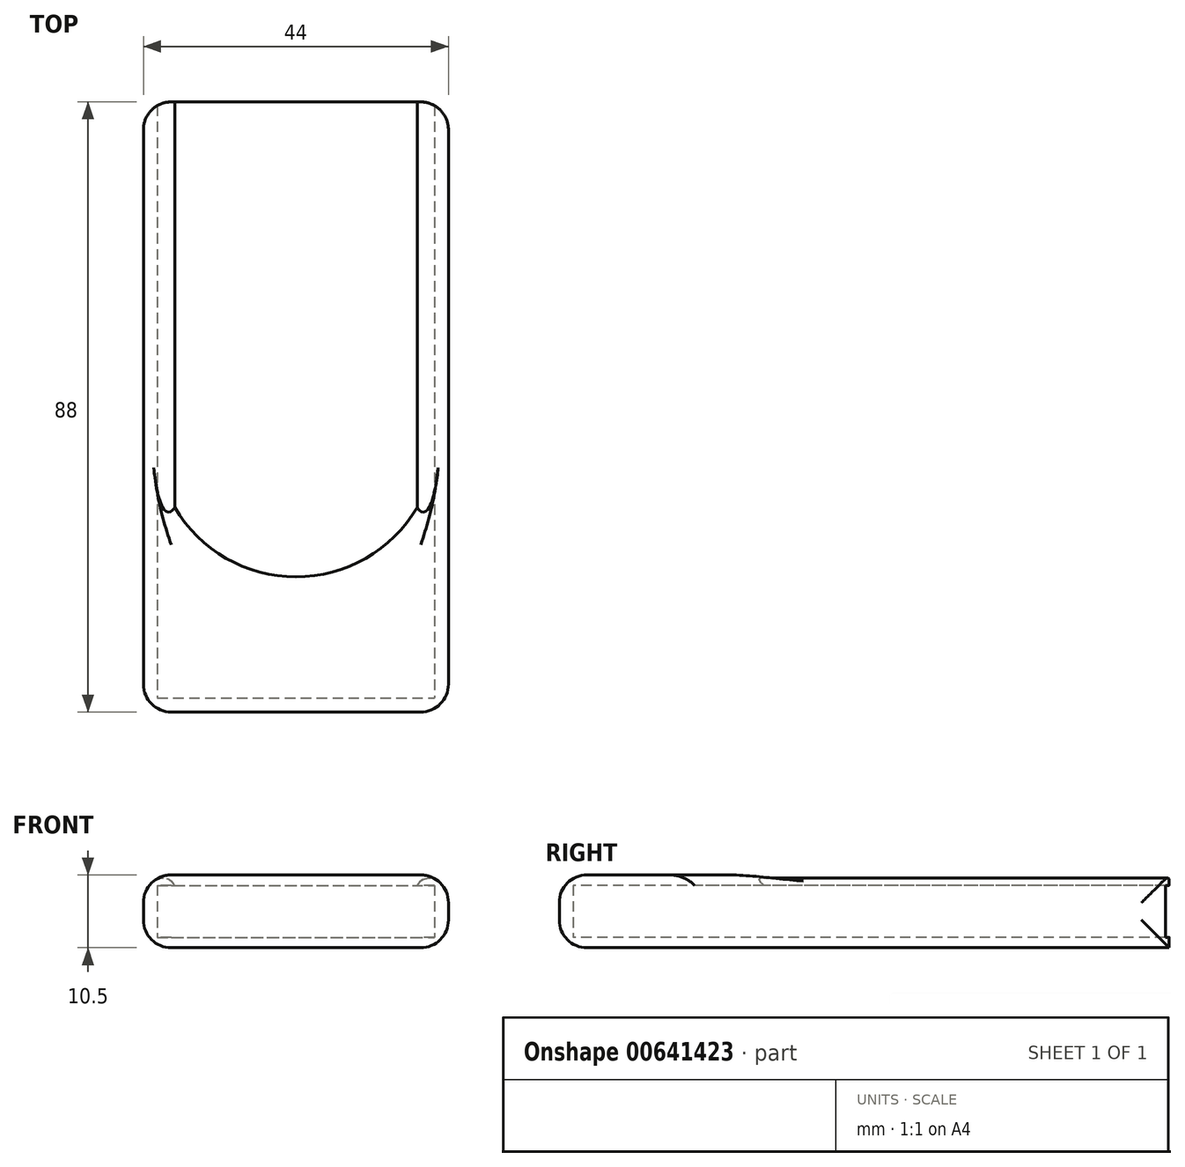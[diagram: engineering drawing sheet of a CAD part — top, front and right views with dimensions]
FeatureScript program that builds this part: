
annotation { "Feature Type Name" : "Feature", "Feature Type Description" : "" }
export const myFeature = defineFeature(function(context is Context, id is Id, definition is map)
    precondition{}
    {
        {
            var Q0;
            Q0=qCreatedBy(makeId("Top.planeOp"),FACE);
            var sketch = newSketch(context, id + "F0", { "sketchPlane" : qUnion([Q0])});
            skLineSegment(sketch, "E0.bottom", {"start": v(-20, 43) * mm, "end": v(20, 43) * mm});
            skLineSegment(sketch, "E0.top", {"start": v(-20, -43) * mm, "end": v(20, -43) * mm});
            skLineSegment(sketch, "E0.left", {"start": v(-20, 43) * mm, "end": v(-20, -43) * mm});
            skLineSegment(sketch, "E0.right", {"start": v(20, 43) * mm, "end": v(20, -43) * mm});
            skPoint(sketch, "E0.middle", {"position": v(0, 0) * mm});
            skLineSegment(sketch, "E1.0", {"start": v(17.5, 43) * mm, "end": v(17.5, -40.5) * mm});
            skLineSegment(sketch, "E1.1", {"start": v(-17.5, -40.5) * mm, "end": v(17.5, -40.5) * mm});
            skLineSegment(sketch, "E1.2", {"start": v(-17.5, 43) * mm, "end": v(-17.5, -40.5) * mm});
            skLineSegment(sketch, "E2.0", {"start": v(22, 43) * mm, "end": v(22, -45) * mm});
            skLineSegment(sketch, "E2.1", {"start": v(-22, -45) * mm, "end": v(22, -45) * mm});
            skLineSegment(sketch, "E2.2", {"start": v(-22, 43) * mm, "end": v(-22, -45) * mm});
            skLineSegment(sketch, "E3", {"start": v(-22, 43) * mm, "end": v(-20, 43) * mm});
            skLineSegment(sketch, "E4", {"start": v(20, 43) * mm, "end": v(22, 43) * mm});
            skArc(sketch, "E5", {"start": v(-17.5, -15.5) * mm, "mid": v(0, -25.5) * mm, "end": v(17.5, -15.5) * mm});
            skSolve(sketch);
        }
        {
            var Q0;
            Q0=makeQuery(id+"F0.imprint","IMPRINT",FACE,{"disambiguationData":[TD([[makeQuery(id+"F0.imprint","IMPRINT",EDGE,{"derivedFrom":sQuery(id+"F0.wireOp",EDGE,"E0.top")}),-1.0]])]});
            var Q1;
            Q1=makeQuery(id+"F0.imprint","IMPRINT",FACE,{"disambiguationData":[TD([[makeQuery(id+"F0.imprint","IMPRINT",EDGE,{"derivedFrom":sQuery(id+"F0.wireOp",EDGE,"E0.top")}),1.0]])]});
            var Q2;
            {var subQ0=sQuery(id+"F0.wireOp",EDGE,"E1.1");Q2=makeQuery(id+"F0.imprint","IMPRINT",FACE,{"disambiguationData":[TD([[makeQuery(id+"F0.imprint","IMPRINT",EDGE,{"derivedFrom":subQ0}),1.0]])]});}
            var Q3;
            {var subQ5=sQuery(id+"F0.wireOp",EDGE,"E5");Q3=makeQuery(id+"F0.imprint","IMPRINT",FACE,{"disambiguationData":[TD([[makeQuery(id+"F0.imprint","IMPRINT",EDGE,{"derivedFrom":subQ5}),1.0]])]});}
            extrude(context, id + "F1", {"entities" : qUnion([Q0, Q1, Q2, Q3]), "oppositeDirection" : true, "depth" : 1.5 * mm, "offsetDistance" : 25 * mm});
        }
        {
            var Q0;
            Q0=makeQuery(id+"F0.imprint","IMPRINT",FACE,{"disambiguationData":[TD([[makeQuery(id+"F0.imprint","IMPRINT",EDGE,{"derivedFrom":sQuery(id+"F0.wireOp",EDGE,"E0.top")}),-1.0]])]});
            var Q1;
            Q1=makeQuery(id+"F0.imprint","IMPRINT",FACE,{"disambiguationData":[TD([[makeQuery(id+"F0.imprint","IMPRINT",EDGE,{"derivedFrom":sQuery(id+"F0.wireOp",EDGE,"E0.top")}),1.0]])]});
            var Q2;
            {var subQ0=sQuery(id+"F0.wireOp",EDGE,"E1.1");Q2=makeQuery(id+"F0.imprint","IMPRINT",FACE,{"disambiguationData":[TD([[makeQuery(id+"F0.imprint","IMPRINT",EDGE,{"derivedFrom":subQ0}),1.0]])]});}
            extrude(context, id + "F2", {"entities" : qUnion([Q0, Q1, Q2]), "operationType" : NewBodyOperationType.ADD, "depth" : 9 * mm, "offsetDistance" : 25 * mm});
        }
        {
            var Q0;
            {var subQ5=sQuery(id+"F0.wireOp",EDGE,"E5");Q0=makeQuery(id+"F0.imprint","IMPRINT",FACE,{"disambiguationData":[TD([[makeQuery(id+"F0.imprint","IMPRINT",EDGE,{"derivedFrom":subQ5}),1.0]])]});}
            var Q1;
            {var subQ0=sQuery(id+"F0.wireOp",EDGE,"E1.1");Q1=makeQuery(id+"F0.imprint","IMPRINT",FACE,{"disambiguationData":[TD([[makeQuery(id+"F0.imprint","IMPRINT",EDGE,{"derivedFrom":subQ0}),1.0]])]});}
            var Q2;
            Q2=makeQuery(id+"F0.imprint","IMPRINT",FACE,{"disambiguationData":[TD([[makeQuery(id+"F0.imprint","IMPRINT",EDGE,{"derivedFrom":sQuery(id+"F0.wireOp",EDGE,"E0.top")}),1.0]])]});
            extrude(context, id + "F3", {"entities" : qUnion([Q0, Q1, Q2]), "operationType" : NewBodyOperationType.REMOVE, "depth" : 7.5 * mm, "offsetDistance" : 25 * mm});
        }
        {
            var Q0;
            {var subQ0=sQuery(id+"F0.wireOp",EDGE,"E2.1");Q0=makeQuery(id+"F2.boolean.opBoolean","MERGE",FACE,{"derivedFrom":[makeQuery(id+"F1.opExtrude","SWEPT_FACE",FACE,{"disambiguationData":[OSD([subQ0])]}),makeQuery(id+"F2.opExtrude","SWEPT_FACE",FACE,{"disambiguationData":[OSD([subQ0])]})]});}
            var Q1;
            {var subQ0=sQuery(id+"F0.wireOp",EDGE,"E2.0");Q1=makeQuery(id+"F2.boolean.opBoolean","MERGE",FACE,{"derivedFrom":[makeQuery(id+"F1.opExtrude","SWEPT_FACE",FACE,{"disambiguationData":[OSD([subQ0])]}),makeQuery(id+"F2.opExtrude","SWEPT_FACE",FACE,{"disambiguationData":[OSD([subQ0])]})]});}
            var Q2;
            {var subQ0=sQuery(id+"F0.wireOp",EDGE,"E2.2");Q2=makeQuery(id+"F2.boolean.opBoolean","MERGE",FACE,{"derivedFrom":[makeQuery(id+"F1.opExtrude","SWEPT_FACE",FACE,{"disambiguationData":[OSD([subQ0])]}),makeQuery(id+"F2.opExtrude","SWEPT_FACE",FACE,{"disambiguationData":[OSD([subQ0])]})]});}
            fillet(context, id + "F4", {"entities" : qUnion([Q0, Q1, Q2]), "radius" : 4 * mm, "tangentPropagation" : true, "allowEdgeOverflow" : false});
        }
        {
            var Q0;
            Q0=makeQuery(id+"F2.opExtrude","CAP_EDGE",EDGE,{"disambiguationData":[OSD([sQuery(id+"F0.wireOp",EDGE,"E5")])],"isStart":false});
            fillet(context, id + "F5", {"entities" : qUnion([Q0]), "radius" : 5 * mm, "tangentPropagation" : true, "allowEdgeOverflow" : false});
        }
        {
            var Q0;
            Q0=makeQuery(id+"F2.opExtrude","CAP_EDGE",EDGE,{"disambiguationData":[OSD([sQuery(id+"F0.wireOp",EDGE,"E1.2")])],"isStart":false});
            fillet(context, id + "F6", {"entities" : qUnion([Q0]), "radius" : 2 * mm, "tangentPropagation" : true, "allowEdgeOverflow" : false});
        }
        {
            var Q0;
            Q0=makeQuery(id+"F2.opExtrude","CAP_EDGE",EDGE,{"disambiguationData":[OSD([sQuery(id+"F0.wireOp",EDGE,"E1.0")])],"isStart":false});
            fillet(context, id + "F7", {"entities" : qUnion([Q0]), "radius" : 2 * mm, "tangentPropagation" : true, "allowEdgeOverflow" : false});
        }
    });
